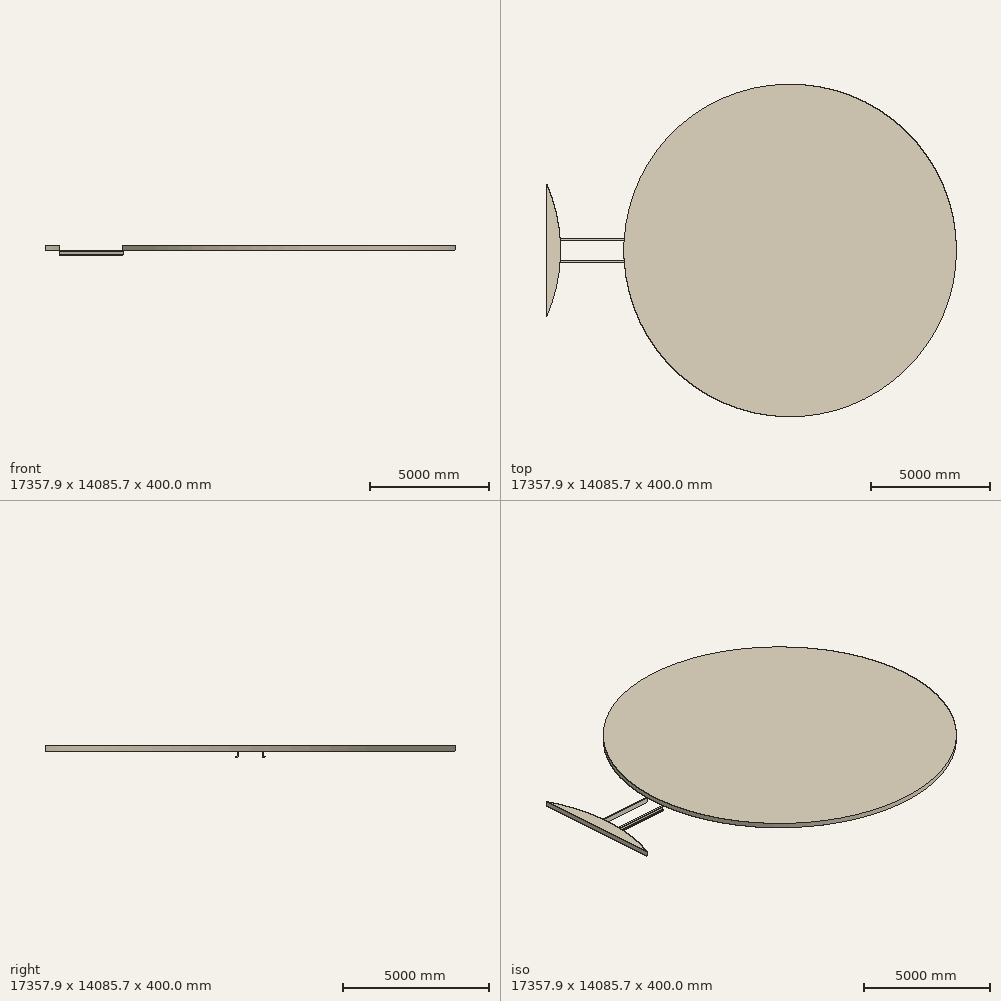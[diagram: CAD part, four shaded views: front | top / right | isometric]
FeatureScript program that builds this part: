
annotation { "Feature Type Name" : "Feature", "Feature Type Description" : "" }
export const myFeature = defineFeature(function(context is Context, id is Id, definition is map)
    precondition{}
    {
        {
            var Q0;
            Q0=qCreatedBy(makeId("Right.planeOp"),FACE);
            var sketch = newSketch(context, id + "F0", { "sketchPlane" : qUnion([Q0])});
            skLineSegment(sketch, "E0", {"start": v(75, 0) * mm, "end": v(0, 0) * mm});
            skLineSegment(sketch, "E1", {"start": v(0, 0) * mm, "end": v(0, -150) * mm});
            skLineSegment(sketch, "E2", {"start": v(0, -150) * mm, "end": v(75, -150) * mm});
            skLineSegment(sketch, "E3", {"start": v(75, -150) * mm, "end": v(75, -140.5) * mm});
            skLineSegment(sketch, "E4", {"start": v(75, -140.5) * mm, "end": v(16, -140.5) * mm});
            skLineSegment(sketch, "E5", {"start": v(75, 0) * mm, "end": v(75, -9.5) * mm});
            skLineSegment(sketch, "E6", {"start": v(75, -9.5) * mm, "end": v(16, -9.5) * mm});
            skLineSegment(sketch, "E7", {"start": v(6, -19.5) * mm, "end": v(6, -130.5) * mm});
            skPoint(sketch, "E8.visualSharp", {"position": v(6, -9.5) * mm});
            skArc(sketch, "E8.filletArc", {"start": v(16, -9.5) * mm, "mid": v(8.93, -12.43) * mm, "end": v(6, -19.5) * mm});
            skPoint(sketch, "E9.visualSharp", {"position": v(6, -140.5) * mm});
            skArc(sketch, "E9.filletArc", {"start": v(6, -130.5) * mm, "mid": v(8.93, -137.57) * mm, "end": v(16, -140.5) * mm});
            skSolve(sketch);
        }
        {
            var Q0;
            Q0=qSketchRegion(id+"F0",true);
            extrude(context, id + "F1", {"entities" : qUnion([Q0]), "endBound" : BoundingType.SYMMETRIC, "depth" : 850 * mm, "offsetDistance" : 25 * mm});
        }
        {
            var Q0;
            Q0=makeQuery(id+"F1.opExtrude","SWEPT_FACE",FACE,{"disambiguationData":[OSD([sQuery(id+"F0.wireOp",EDGE,"E1")])]});
            var sketch = newSketch(context, id + "F2", { "sketchPlane" : qUnion([Q0])});
            skCircle(sketch, "E10", {"center": v(-375, -75) * mm, "radius": 9 * mm});
            skCircle(sketch, "E11", {"center": v(-225, -75) * mm, "radius": 9 * mm});
            skCircle(sketch, "E12", {"center": v(225, -75) * mm, "radius": 9 * mm});
            skCircle(sketch, "E13", {"center": v(375, -75) * mm, "radius": 9 * mm});
            skSolve(sketch);
        }
        {
            var Q0;
            Q0=qCreatedBy(makeId("Right.planeOp"),FACE);
            var sketch = newSketch(context, id + "F3", { "sketchPlane" : qUnion([Q0])});
            skLineSegment(sketch, "E14", {"start": v(69, 25) * mm, "end": v(-6, 25) * mm});
            skLineSegment(sketch, "E15", {"start": v(-6, 25) * mm, "end": v(-6, -175) * mm});
            skLineSegment(sketch, "E16", {"start": v(-6, -175) * mm, "end": v(69, -175) * mm});
            skLineSegment(sketch, "E17", {"start": v(69, -175) * mm, "end": v(69, -163) * mm});
            skLineSegment(sketch, "E18", {"start": v(69, -163) * mm, "end": v(12, -163) * mm});
            skLineSegment(sketch, "E19", {"start": v(0, -151) * mm, "end": v(0, 1) * mm});
            skLineSegment(sketch, "E20", {"start": v(12, 13) * mm, "end": v(69, 13) * mm});
            skLineSegment(sketch, "E21", {"start": v(69, 13) * mm, "end": v(69, 25) * mm});
            skPoint(sketch, "E22.visualSharp", {"position": v(0, 13) * mm});
            skArc(sketch, "E22.filletArc", {"start": v(12, 13) * mm, "mid": v(3.51, 9.49) * mm, "end": v(0, 1) * mm});
            skPoint(sketch, "E23.visualSharp", {"position": v(0, -163) * mm});
            skArc(sketch, "E23.filletArc", {"start": v(0, -151) * mm, "mid": v(3.51, -159.49) * mm, "end": v(12, -163) * mm});
            skPoint(sketch, "E24", {"position": v(0, -75) * mm});
            skSolve(sketch);
        }
        {
            var Q0;
            Q0 = qSketchRegion(id + "F3", true);
            extrude(context, id + "F4", {"entities" : qUnion([Q0]), "operationType" : NewBodyOperationType.ADD, "oppositeDirection" : true, "depth" : 700 * mm, "offsetDistance" : 25 * mm, "hasSecondDirection" : true, "secondDirectionOppositeDirection" : false, "secondDirectionDepth" : 2000 * mm});
        }
        {
            var Q0;
            Q0=qCreatedBy(makeId("Right.planeOp"),FACE);
            var sketch = newSketch(context, id + "F5", { "sketchPlane" : qUnion([Q0])});
            skLineSegment(sketch, "E25", {"start": v(-931, -175) * mm, "end": v(-856, -175) * mm});
            skLineSegment(sketch, "E26", {"start": v(-856, -175) * mm, "end": v(-856, 25) * mm});
            skLineSegment(sketch, "E27", {"start": v(-856, 25) * mm, "end": v(-931, 25) * mm});
            skLineSegment(sketch, "E28", {"start": v(-931, 25) * mm, "end": v(-931, 13) * mm});
            skLineSegment(sketch, "E29", {"start": v(-931, 13) * mm, "end": v(-874, 13) * mm});
            skLineSegment(sketch, "E30", {"start": v(-862, 1) * mm, "end": v(-862, -151) * mm});
            skLineSegment(sketch, "E31", {"start": v(-874, -163) * mm, "end": v(-931, -163) * mm});
            skLineSegment(sketch, "E32", {"start": v(-931, -163) * mm, "end": v(-931, -175) * mm});
            skPoint(sketch, "E33.visualSharp", {"position": v(-862, -163) * mm});
            skArc(sketch, "E33.filletArc", {"start": v(-874, -163) * mm, "mid": v(-865.51, -159.49) * mm, "end": v(-862, -151) * mm});
            skPoint(sketch, "E34.visualSharp", {"position": v(-862, 13) * mm});
            skArc(sketch, "E34.filletArc", {"start": v(-862, 1) * mm, "mid": v(-865.51, 9.49) * mm, "end": v(-874, 13) * mm});
            skPoint(sketch, "E35", {"position": v(-862, -75) * mm});
            skSolve(sketch);
        }
        {
            var Q0;
            Q0 = qSketchRegion(id + "F5", true);
            extrude(context, id + "F6", {"entities" : qUnion([Q0]), "oppositeDirection" : true, "depth" : 700 * mm, "offsetDistance" : 25 * mm, "hasSecondDirection" : true, "secondDirectionOppositeDirection" : false, "secondDirectionDepth" : 2000 * mm});
        }
        {
            var Q0;
            Q0=makeQuery(id+"F4.opExtrude","SWEPT_FACE",FACE,{"disambiguationData":[OSD([sQuery(id+"F3.wireOp",EDGE,"E14")])]});
            var sketch = newSketch(context, id + "F7", { "sketchPlane" : qUnion([Q0])});
            skPoint(sketch, "E36", {"position": v(650, 69) * mm});
            skLineSegment(sketch, "E37", {"start": v(650, 69) * mm, "end": v(650, -931) * mm, "construction": true});
            skLineSegment(sketch, "E38.0", {"start": v(-7730, 69) * mm, "end": v(-7730, -931) * mm, "construction": true});
            skPoint(sketch, "E39", {"position": v(-7730, -431) * mm});
            skArc(sketch, "E40", {"start": v(-1285.1, -3270.84) * mm, "mid": v(-687.16, -431) * mm, "end": v(-1285.1, 2408.84) * mm});
            skCircle(sketch, "E41", {"center": v(9030, -431) * mm, "radius": 7042.84 * mm});
            skLineSegment(sketch, "E42", {"start": v(-1285.1, 2408.84) * mm, "end": v(-1285.1, -3270.84) * mm});
            skSolve(sketch);
        }
        {
            var Q0;
            Q0 = qSketchRegion(id + "F7", true);
            extrude(context, id + "F8", {"entities" : qUnion([Q0]), "depth" : 200 * mm, "offsetDistance" : 25 * mm});
        }
    });
